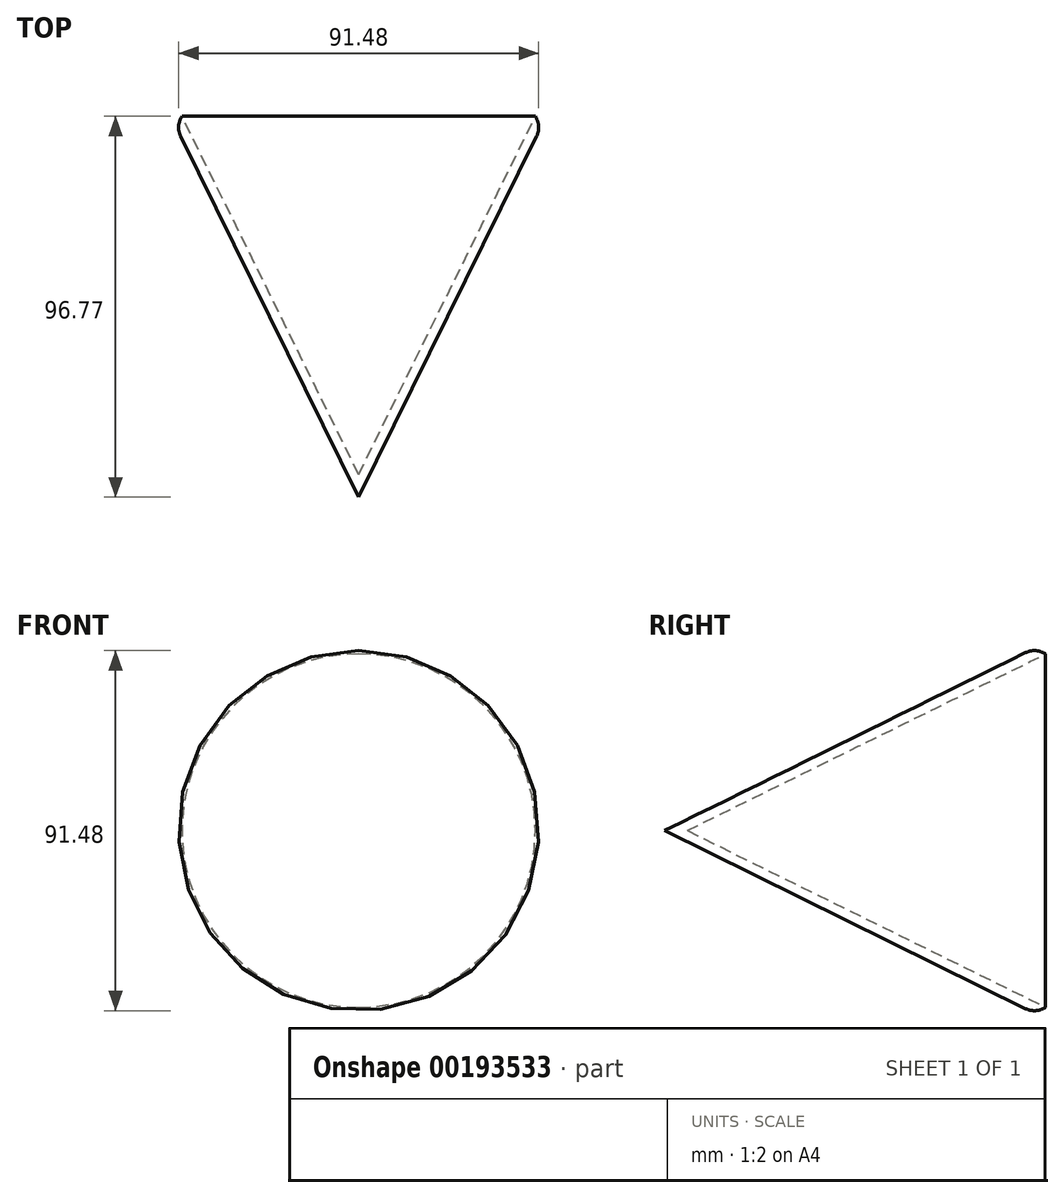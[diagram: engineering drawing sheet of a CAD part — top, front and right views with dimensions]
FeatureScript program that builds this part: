
annotation { "Feature Type Name" : "Feature", "Feature Type Description" : "" }
export const myFeature = defineFeature(function(context is Context, id is Id, definition is map)
    precondition{}
    {
        {
            var Q0;
            Q0=qCreatedBy(makeId("Top.planeOp"),FACE);
            var sketch = newSketch(context, id + "F0", { "sketchPlane" : qUnion([Q0])});
            skLineSegment(sketch, "E0", {"start": v(0, 44.85) * mm, "end": v(0, -49.27) * mm});
            skLineSegment(sketch, "E1", {"start": v(0, -49.27) * mm, "end": v(47.72, 47.5) * mm});
            skLineSegment(sketch, "E2", {"start": v(47.72, 47.5) * mm, "end": v(0, 47.5) * mm});
            skLineSegment(sketch, "E3", {"start": v(0, 47.5) * mm, "end": v(0, 44.85) * mm});
            skSolve(sketch);
        }
        {
            var Q0;
            Q0=makeQuery(id+"F0.imprint","IMPRINT",FACE,{"disambiguationData":[TD([[makeQuery(id+"F0.imprint","IMPRINT",EDGE,{"derivedFrom":sQuery(id+"F0.wireOp",EDGE,"E0")}),1.0]])]});
            var Q1;
            Q1=sQuery(id+"F0.wireOp",EDGE,"E0");
            revolve(context, id + "F1", {"entities" : qUnion([Q0]), "axis" : qUnion([Q1]), "revolveType" : RevolveType.FULL});
        }
        {
            var Q0;
            Q0=makeQuery(id+"F1.opRevolve","SWEPT_FACE",FACE,{"disambiguationData":[OSD([sQuery(id+"F0.wireOp",EDGE,"E2")])]});
            shell(context, id + "F2", {"entities" : qUnion([Q0]), "thickness" : 2.54 * mm});
        }
        {
            var Q0;
            Q0=makeQuery(id+"F1.opRevolve","SWEPT_EDGE",EDGE,{"disambiguationData":[OSD([sQuery(id+"F0.wireOp",EDGE,"E1"),sQuery(id+"F0.wireOp",EDGE,"E2")])]});
            fillet(context, id + "F3", {"entities" : qUnion([Q0]), "radius" : 5.08 * mm, "tangentPropagation" : true, "allowEdgeOverflow" : false});
        }
    });
